FCSTD DOCUMENT  (FreeCAD 0.20R0.20)
Label: 003
License: All rights reserved
LicenseURL: http://en.wikipedia.org/wiki/All_rights_reserved
objects: Sketcher::SketchObject×1
note: 1 computed .brp shape members not serialized (recipe doc carries the construction recipe); baked Part::Feature solids carry a one-line shape summary decoded from their .brp

FEATURE [Sketcher::SketchObject] Sketch
  FullyConstrained = true
  sketch-geometry (10):
    g0: LineSegment StartX=0 StartY=0 StartZ=0 EndX=0 EndY=23 EndZ=0
    g1: LineSegment StartX=0 StartY=0 StartZ=0 EndX=28 EndY=0 EndZ=0
    g2: LineSegment StartX=0 StartY=23 StartZ=0 EndX=24 EndY=23 EndZ=0
    g3: LineSegment StartX=24 StartY=23 StartZ=0 EndX=24 EndY=16 EndZ=0
    g4: LineSegment StartX=28 StartY=0 StartZ=0 EndX=28 EndY=-2 EndZ=0
    g5: LineSegment StartX=28 StartY=-2 StartZ=0 EndX=-2 EndY=-2 EndZ=0
    g6: LineSegment StartX=-2 StartY=-2 StartZ=0 EndX=-2 EndY=25 EndZ=0
    g7: LineSegment StartX=-2 StartY=25 StartZ=0 EndX=26 EndY=25 EndZ=0
    g8: LineSegment StartX=26 StartY=25 StartZ=0 EndX=26 EndY=16 EndZ=0
    g9: LineSegment StartX=24 StartY=16 StartZ=0 EndX=26 EndY=16 EndZ=0
  constraints (31):
    c: Coincident(g0,g-1)
    c: Vertical(g0)
    c: Distance(g0) = 23
    c: Coincident(g1,g0)
    c: Horizontal(g1)
    c: Distance(g1) = 28
    c: Coincident(g2,g0)
    c: Horizontal(g2)
    c: Block(g2)
    c: Block(g0)
    c: Block(g1)
    c: Coincident(g3,g2)
    c: Vertical(g3)
    c: Distance(g3) = 7
    c: Coincident(g4,g1)
    c: Vertical(g4)
    c: Distance(g4) = 2
    c: Coincident(g5,g4)
    c: Horizontal(g5)
    c: Distance(g5) = 30
    c: Coincident(g6,g5)
    c: Vertical(g6)
    c: Distance(g6) = 27
    c: Coincident(g7,g6)
    c: Horizontal(g7)
    c: Distance(g7) = 28
    c: Coincident(g8,g7)
    c: Vertical(g8)
    c: Coincident(g9,g3)
    c: Horizontal(g9)
    c: Coincident(g8,g9)
